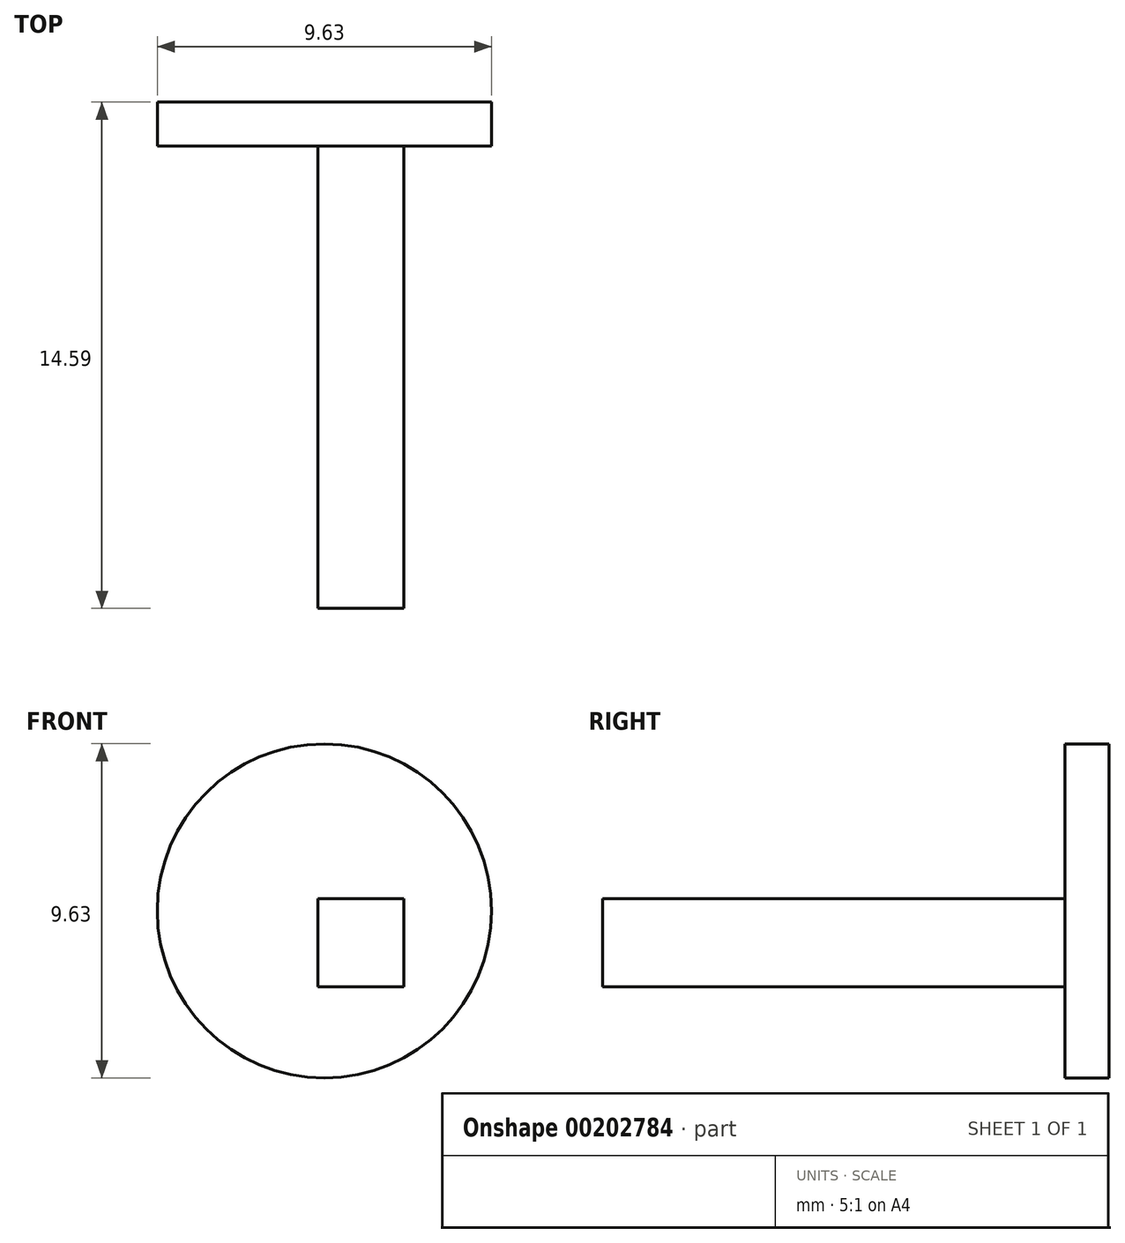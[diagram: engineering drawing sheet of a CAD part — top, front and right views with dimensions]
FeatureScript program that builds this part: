
annotation { "Feature Type Name" : "Feature", "Feature Type Description" : "" }
export const myFeature = defineFeature(function(context is Context, id is Id, definition is map)
    precondition{}
    {
        {
            var Q0;
            Q0=qCreatedBy(makeId("Top.planeOp"),FACE);
            var sketch = newSketch(context, id + "F0", { "sketchPlane" : qUnion([Q0])});
            skLineSegment(sketch, "E0", {"start": v(-2.48, 0) * mm, "end": v(-2.48, -14.6) * mm});
            skLineSegment(sketch, "E1", {"start": v(-2.48, -14.6) * mm, "end": v(0, -14.6) * mm});
            skLineSegment(sketch, "E2", {"start": v(0, 0) * mm, "end": v(0, -14.6) * mm});
            skLineSegment(sketch, "E3", {"start": v(-2.48, 0) * mm, "end": v(0, 0) * mm});
            skSolve(sketch);
        }
        {
            var Q0;
            Q0=makeQuery(id+"F0.imprint","IMPRINT",FACE,{"disambiguationData":[TD([[makeQuery(id+"F0.imprint","IMPRINT",EDGE,{"derivedFrom":sQuery(id+"F0.wireOp",EDGE,"E0")}),1.0]])]});
            extrude(context, id + "F1", {"entities" : qUnion([Q0]), "depth" : 2.54 * mm});
        }
        {
            var Q0;
            Q0=qCreatedBy(makeId("Front.planeOp"),FACE);
            var sketch = newSketch(context, id + "F2", { "sketchPlane" : qUnion([Q0])});
            skCircle(sketch, "E4", {"center": v(-2.29, 2.2) * mm, "radius": 4.81 * mm});
            skSolve(sketch);
        }
        {
            var Q0;
            Q0=makeQuery(id+"F2.imprint","IMPRINT",FACE,{"disambiguationData":[TD([[makeQuery(id+"F2.imprint","IMPRINT",EDGE,{"derivedFrom":sQuery(id+"F2.wireOp",EDGE,"E4")}),1.0]])]});
            extrude(context, id + "F3", {"entities" : qUnion([Q0]), "operationType" : NewBodyOperationType.ADD, "depth" : 1.27 * mm});
        }
    });
